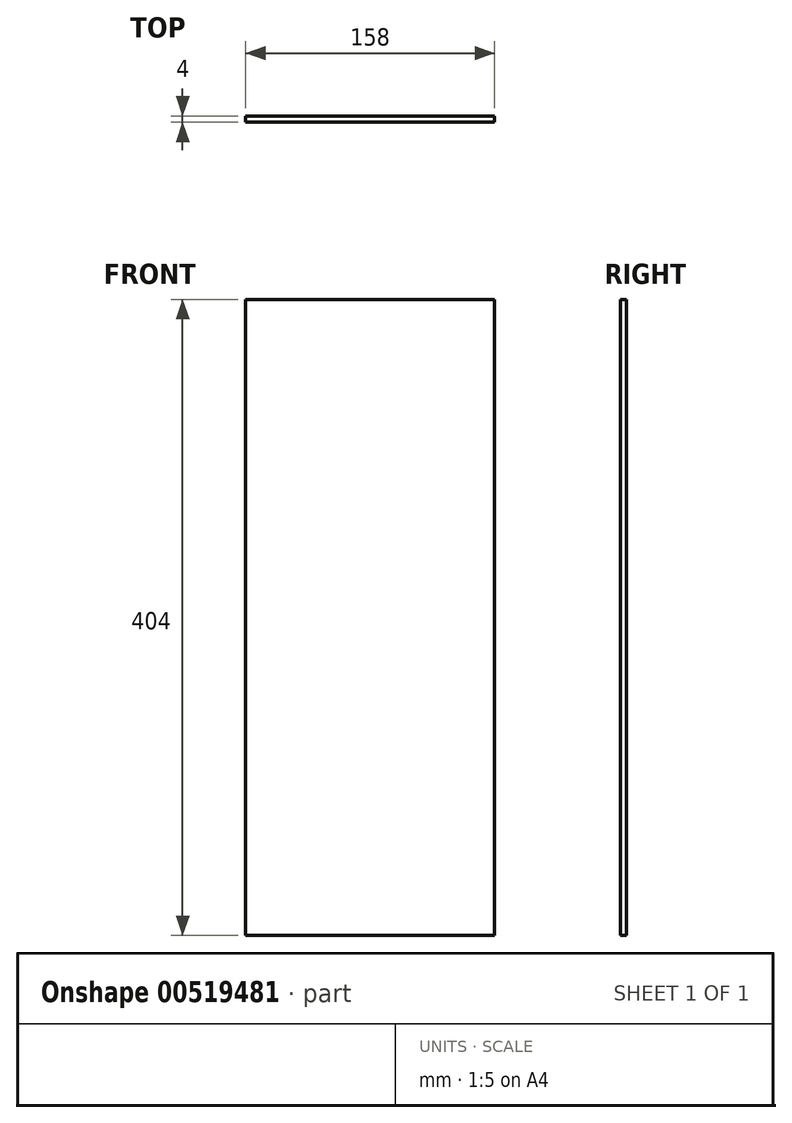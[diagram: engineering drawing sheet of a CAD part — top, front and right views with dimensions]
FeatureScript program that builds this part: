
annotation { "Feature Type Name" : "Feature", "Feature Type Description" : "" }
export const myFeature = defineFeature(function(context is Context, id is Id, definition is map)
    precondition{}
    {
        {
            var Q0;
            Q0=qCreatedBy(makeId("Front.planeOp"),FACE);
            var sketch = newSketch(context, id + "F0", { "sketchPlane" : qUnion([Q0])});
            skLineSegment(sketch, "E0", {"start": v(0, 0) * mm, "end": v(158, 0) * mm});
            skLineSegment(sketch, "E1", {"start": v(0, 404) * mm, "end": v(0, 0) * mm});
            skLineSegment(sketch, "E2", {"start": v(158, 0) * mm, "end": v(158, 404) * mm});
            skLineSegment(sketch, "E3", {"start": v(158, 404) * mm, "end": v(0, 404) * mm});
            skSolve(sketch);
        }
        {
            var Q0;
            Q0=makeQuery(id+"F0.imprint","IMPRINT",FACE,{"disambiguationData":[TD([[makeQuery(id+"F0.imprint","IMPRINT",EDGE,{"derivedFrom":sQuery(id+"F0.wireOp",EDGE,"E0")}),1.0]])]});
            extrude(context, id + "F1", {"entities" : qUnion([Q0]), "depth" : 4 * mm, "offsetDistance" : 25 * mm});
        }
    });
